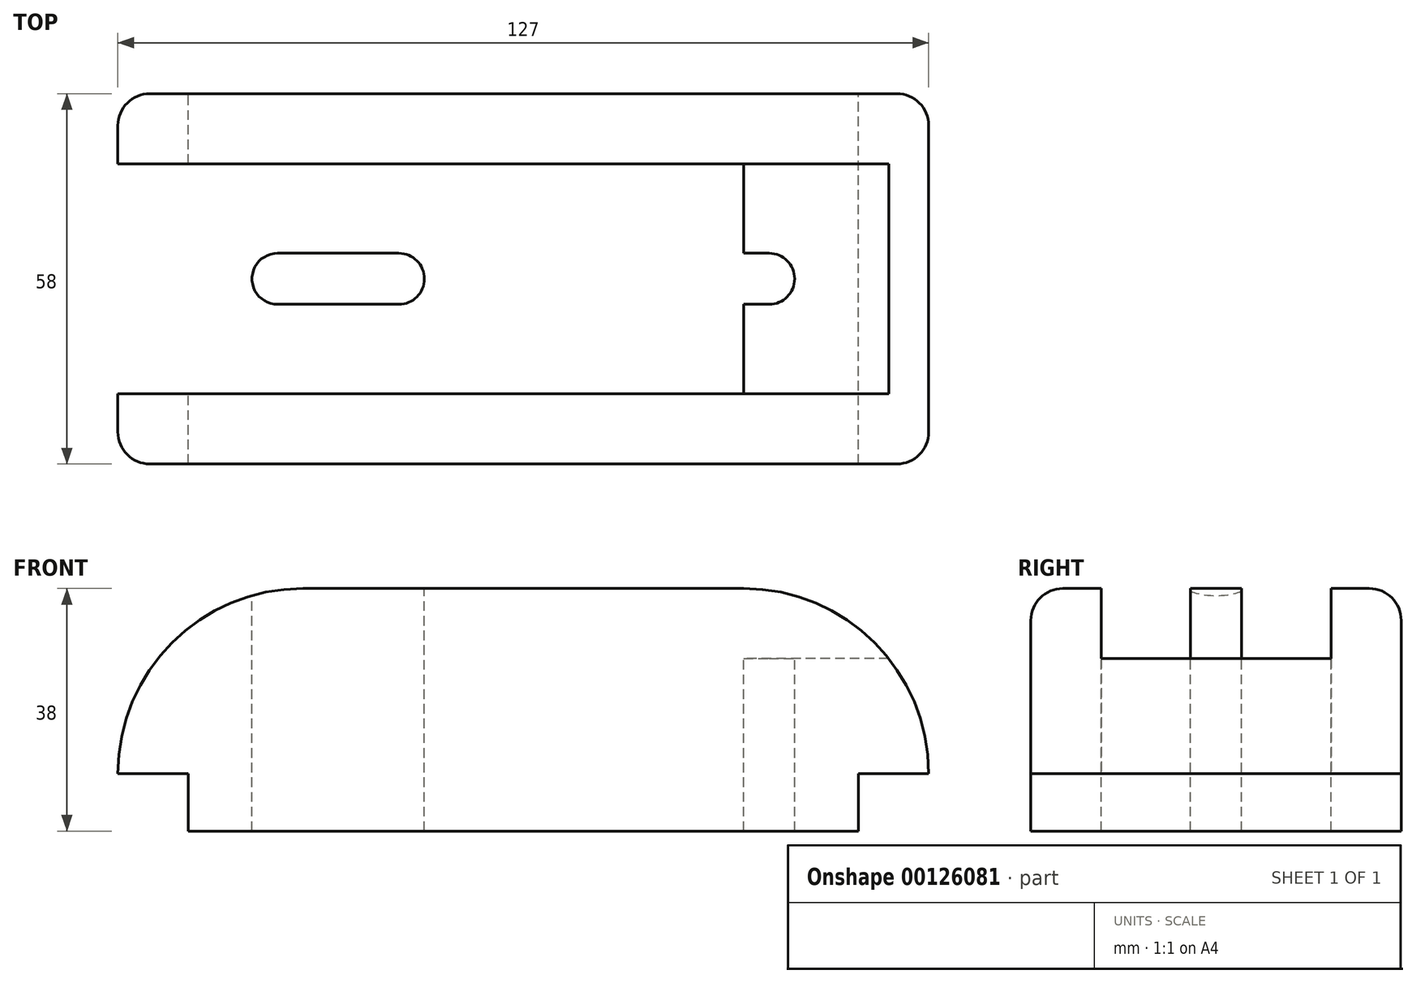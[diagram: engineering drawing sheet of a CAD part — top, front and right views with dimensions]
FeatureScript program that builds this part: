
annotation { "Feature Type Name" : "Feature", "Feature Type Description" : "" }
export const myFeature = defineFeature(function(context is Context, id is Id, definition is map)
    precondition{}
    {
        {
            var Q0;
            Q0=qCreatedBy(makeId("Front.planeOp"),FACE);
            var sketch = newSketch(context, id + "F0", { "sketchPlane" : qUnion([Q0])});
            skLineSegment(sketch, "E0", {"start": v(0, 0) * mm, "end": v(52.5, 0) * mm});
            skLineSegment(sketch, "E1", {"start": v(52.5, 0) * mm, "end": v(52.5, 9) * mm});
            skLineSegment(sketch, "E2", {"start": v(52.5, 9) * mm, "end": v(63.5, 9) * mm});
            skLineSegment(sketch, "E3", {"start": v(0, 38) * mm, "end": v(34.5, 38) * mm});
            skArc(sketch, "E4", {"start": v(63.5, 9) * mm, "mid": v(55, 29.5) * mm, "end": v(34.5, 38) * mm});
            skLineSegment(sketch, "E5.MirrorCS", {"start": v(0, 38) * mm, "end": v(-34.5, 38) * mm});
            skArc(sketch, "E6.MirrorCS", {"start": v(-63.5, 9) * mm, "mid": v(-55, 29.5) * mm, "end": v(-34.5, 38) * mm});
            skLineSegment(sketch, "E7.MirrorCS", {"start": v(-52.5, 9) * mm, "end": v(-63.5, 9) * mm});
            skLineSegment(sketch, "E8.MirrorCS", {"start": v(0, 0) * mm, "end": v(-52.5, 0) * mm});
            skLineSegment(sketch, "E9.MirrorCS", {"start": v(-52.5, 0) * mm, "end": v(-52.5, 9) * mm});
            skSolve(sketch);
        }
        {
            var Q0;
            Q0 = qSketchRegion(id + "F0", true);
            extrude(context, id + "F1", {"entities" : qUnion([Q0]), "endBound" : BoundingType.SYMMETRIC, "depth" : 58 * mm});
        }
        {
            var Q0;
            Q0=makeQuery(id+"F1.opExtrude","SWEPT_FACE",FACE,{"disambiguationData":[OSD([sQuery(id+"F0.wireOp",EDGE,"E3"),sQuery(id+"F0.wireOp",EDGE,"E5.MirrorCS")])]});
            var sketch = newSketch(context, id + "F2", { "sketchPlane" : qUnion([Q0])});
            skLineSegment(sketch, "E10.bottom", {"start": v(-34.5, 18) * mm, "end": v(34.5, 18) * mm});
            skLineSegment(sketch, "E10.top", {"start": v(-34.5, -18) * mm, "end": v(34.5, -18) * mm});
            skLineSegment(sketch, "E10.left", {"start": v(-34.5, 18) * mm, "end": v(-34.5, -18) * mm});
            skLineSegment(sketch, "E10.right", {"start": v(34.5, 18) * mm, "end": v(34.5, -18) * mm});
            skLineSegment(sketch, "E11.bottom", {"start": v(34.5, 18) * mm, "end": v(74.5, 18) * mm});
            skLineSegment(sketch, "E11.top", {"start": v(34.5, -18) * mm, "end": v(74.5, -18) * mm});
            skLineSegment(sketch, "E11.right", {"start": v(74.5, 18) * mm, "end": v(74.5, -18) * mm});
            skLineSegment(sketch, "E12.bottom", {"start": v(-34.5, 18) * mm, "end": v(-67.5, 18) * mm});
            skLineSegment(sketch, "E12.top", {"start": v(-34.5, -18) * mm, "end": v(-67.5, -18) * mm});
            skLineSegment(sketch, "E12.right", {"start": v(-67.5, 18) * mm, "end": v(-67.5, -18) * mm});
            skPoint(sketch, "E13", {"position": v(-34.5, 0) * mm});
            skLineSegment(sketch, "E14", {"start": v(-34.5, 0) * mm, "end": v(-34.5, 0) * mm});
            skLineSegment(sketch, "E15", {"start": v(19.5, -4) * mm, "end": v(38.5, -4) * mm});
            skLineSegment(sketch, "E16", {"start": v(19.5, 4) * mm, "end": v(38.5, 4) * mm});
            skArc(sketch, "E17", {"start": v(19.5, 4) * mm, "mid": v(15.5, 0) * mm, "end": v(19.5, -4) * mm});
            skArc(sketch, "E18", {"start": v(38.5, -4) * mm, "mid": v(42.5, 0) * mm, "end": v(38.5, 4) * mm});
            skLineSegment(sketch, "E19", {"start": v(29, -4) * mm, "end": v(29, -29) * mm, "construction": true});
            skLineSegment(sketch, "E20", {"start": v(29, 4) * mm, "end": v(29, 29) * mm, "construction": true});
            skArc(sketch, "E21.MirrorCS", {"start": v(-19.5, 4) * mm, "mid": v(-15.5, 0) * mm, "end": v(-19.5, -4) * mm});
            skLineSegment(sketch, "E22.MirrorCS", {"start": v(-19.5, -4) * mm, "end": v(-38.5, -4) * mm});
            skLineSegment(sketch, "E23.MirrorCS", {"start": v(-19.5, 4) * mm, "end": v(-38.5, 4) * mm});
            skArc(sketch, "E24.MirrorCS", {"start": v(-38.5, -4) * mm, "mid": v(-42.5, 0) * mm, "end": v(-38.5, 4) * mm});
            skSolve(sketch);
        }
        {
            var Q0;
            {var subQ5=sQuery(id+"F2.wireOp",EDGE,"E21.MirrorCS");Q0=makeQuery(id+"F2.imprint","IMPRINT",FACE,{"disambiguationData":[TD([[makeQuery(id+"F2.imprint","IMPRINT",EDGE,{"derivedFrom":subQ5}),-1.0]])]});}
            var Q1;
            {var subQ5=sQuery(id+"F2.wireOp",EDGE,"E24.MirrorCS");Q1=makeQuery(id+"F2.imprint","IMPRINT",FACE,{"disambiguationData":[TD([[makeQuery(id+"F2.imprint","IMPRINT",EDGE,{"derivedFrom":subQ5}),-1.0]])]});}
            var Q2;
            {var subQ5=sQuery(id+"F2.wireOp",EDGE,"E17");Q2=makeQuery(id+"F2.imprint","IMPRINT",FACE,{"disambiguationData":[TD([[makeQuery(id+"F2.imprint","IMPRINT",EDGE,{"derivedFrom":subQ5}),1.0]])]});}
            var Q3;
            {var subQ5=sQuery(id+"F2.wireOp",EDGE,"E18");Q3=makeQuery(id+"F2.imprint","IMPRINT",FACE,{"disambiguationData":[TD([[makeQuery(id+"F2.imprint","IMPRINT",EDGE,{"derivedFrom":subQ5}),1.0]])]});}
            extrude(context, id + "F3", {"entities" : qUnion([Q0, Q1, Q2, Q3]), "operationType" : NewBodyOperationType.REMOVE, "endBound" : BoundingType.THROUGH_ALL, "oppositeDirection" : true, "depth" : 25 * mm});
        }
        {
            var Q0;
            {var subQ1=sQuery(id+"F2.wireOp",EDGE,"E12.bottom");Q0=makeQuery(id+"F2.imprint","IMPRINT",FACE,{"disambiguationData":[TD([[makeQuery(id+"F2.imprint","IMPRINT",EDGE,{"derivedFrom":subQ1}),1.0]])]});}
            var Q1;
            {var subQ1=sQuery(id+"F2.wireOp",EDGE,"E10.bottom");Q1=makeQuery(id+"F2.imprint","IMPRINT",FACE,{"disambiguationData":[TD([[makeQuery(id+"F2.imprint","IMPRINT",EDGE,{"derivedFrom":subQ1}),-1.0]])]});}
            var Q2;
            {var subQ1=sQuery(id+"F2.wireOp",EDGE,"E11.bottom");Q2=makeQuery(id+"F2.imprint","IMPRINT",FACE,{"disambiguationData":[TD([[makeQuery(id+"F2.imprint","IMPRINT",EDGE,{"derivedFrom":subQ1}),-1.0]])]});}
            extrude(context, id + "F4", {"entities" : qUnion([Q0, Q1, Q2]), "operationType" : NewBodyOperationType.REMOVE, "oppositeDirection" : true, "depth" : 11 * mm});
        }
        {
            var Q0;
            Q0=makeQuery(id+"F1.opExtrude","CAP_EDGE",EDGE,{"disambiguationData":[OSD([sQuery(id+"F0.wireOp",EDGE,"E3"),sQuery(id+"F0.wireOp",EDGE,"E5.MirrorCS")])],"isStart":false});
            var Q1;
            Q1=makeQuery(id+"F1.opExtrude","CAP_EDGE",EDGE,{"disambiguationData":[OSD([sQuery(id+"F0.wireOp",EDGE,"E3"),sQuery(id+"F0.wireOp",EDGE,"E5.MirrorCS")])],"isStart":true});
            fillet(context, id + "F5", {"entities" : qUnion([Q0, Q1]), "radius" : 5 * mm, "tangentPropagation" : true, "allowEdgeOverflow" : false});
        }
    });
